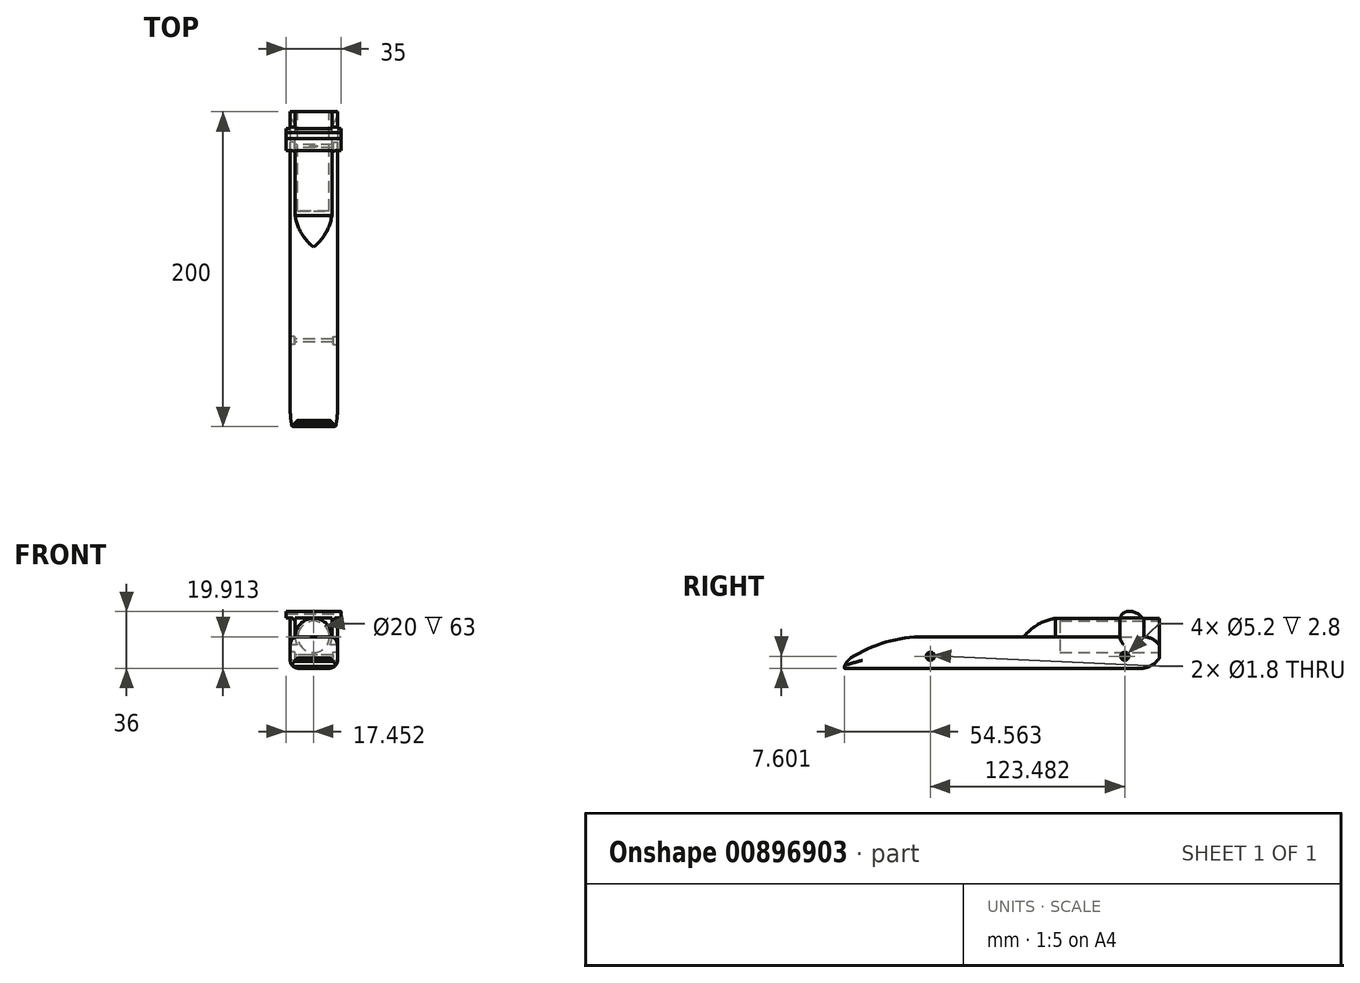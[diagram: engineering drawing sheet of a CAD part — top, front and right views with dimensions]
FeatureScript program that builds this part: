
annotation { "Feature Type Name" : "Feature", "Feature Type Description" : "" }
export const myFeature = defineFeature(function(context is Context, id is Id, definition is map)
    precondition{}
    {
        {
            var Q0;
            Q0=qCreatedBy(makeId("Right.planeOp"),FACE);
            var sketch = newSketch(context, id + "F0", { "sketchPlane" : qUnion([Q0])});
            skLineSegment(sketch, "E0.bottom", {"start": v(89.71, -10) * mm, "end": v(-37.4, -10) * mm});
            skLineSegment(sketch, "E0.top", {"start": v(90.1, 10) * mm, "end": v(-49.28, 10) * mm});
            skLineSegment(sketch, "E0.left", {"start": v(100, -3.63) * mm, "end": v(100, 4.7) * mm});
            skPoint(sketch, "E0.middle", {"position": v(0, 0) * mm});
            skArc(sketch, "E1", {"start": v(-32.94, 10) * mm, "mid": v(-41.11, 10.16) * mm, "end": v(-49.28, 10) * mm});
            skArc(sketch, "E2", {"start": v(-37.4, -10) * mm, "mid": v(-35.18, -10.01) * mm, "end": v(-32.94, -10) * mm});
            skPoint(sketch, "E3.orphan", {"position": v(-100, 10) * mm});
            skPoint(sketch, "E4.orphan", {"position": v(-100, -10) * mm});
            skCircle(sketch, "E5", {"center": v(78.04, -2.4) * mm, "radius": 0.9 * mm});
            skCircle(sketch, "E6", {"center": v(-45.44, -2.4) * mm, "radius": 0.9 * mm});
            skArc(sketch, "E7", {"start": v(100, 4.7) * mm, "mid": v(95.32, 8.7) * mm, "end": v(89.32, 10) * mm});
            skArc(sketch, "E8", {"start": v(89.71, -10) * mm, "mid": v(95.52, -7.9) * mm, "end": v(100, -3.63) * mm});
            skPoint(sketch, "E9.orphan", {"position": v(100, 10) * mm});
            skPoint(sketch, "E10.orphan", {"position": v(100, -10) * mm});
            skLineSegment(sketch, "E11", {"start": v(-37.4, -10) * mm, "end": v(-100, -10) * mm});
            skPoint(sketch, "E0.right.start.orphan", {"position": v(-100, 0) * mm});
            skArc(sketch, "E12", {"start": v(-49.28, 10) * mm, "mid": v(-75.9, 5.84) * mm, "end": v(-100, -6.23) * mm});
            skLineSegment(sketch, "E13", {"start": v(-100, -6.23) * mm, "end": v(-100, -10) * mm});
            skSolve(sketch);
        }
        {
            var Q0;
            {var subQ4=sQuery(id+"F0.wireOp",EDGE,"E0.left");Q0=makeQuery(id+"F0.imprint","IMPRINT",FACE,{"disambiguationData":[TD([[makeQuery(id+"F0.imprint","IMPRINT",EDGE,{"derivedFrom":subQ4}),1.0]])]});}
            extrude(context, id + "F1", {"entities" : qUnion([Q0]), "depth" : 30 * mm, "offsetDistance" : 25 * mm});
        }
        {
            var Q0;
            Q0=makeQuery(id+"F1.opExtrude","SWEPT_FACE",FACE,{"disambiguationData":[OSD([sQuery(id+"F0.wireOp",EDGE,"E0.left")])]});
            var sketch = newSketch(context, id + "F2", { "sketchPlane" : qUnion([Q0])});
            skCircle(sketch, "E14", {"center": v(-14.8, 9.91) * mm, "radius": 11.67 * mm});
            skSolve(sketch);
        }
        {
            var Q0;
            Q0=qSketchRegion(id+"F2",true);
            extrude(context, id + "F3", {"entities" : qUnion([Q0]), "operationType" : NewBodyOperationType.ADD, "oppositeDirection" : true, "depth" : 66 * mm, "offsetDistance" : 25 * mm});
        }
        {
            var Q0;
            Q0=makeQuery(id+"F3.opExtrude","CAP_FACE",FACE,{"disambiguationData":[OSD([sQuery(id+"F2.wireOp",EDGE,"E14")])],"isStart":true});
            var sketch = newSketch(context, id + "F4", { "sketchPlane" : qUnion([Q0])});
            skCircle(sketch, "E15", {"center": v(-14.8, 9.91) * mm, "radius": 10 * mm});
            skSolve(sketch);
        }
        {
            var Q0;
            Q0=qSketchRegion(id+"F4",true);
            extrude(context, id + "F5", {"entities" : qUnion([Q0]), "operationType" : NewBodyOperationType.REMOVE, "oppositeDirection" : true, "depth" : 63 * mm, "offsetDistance" : 25 * mm});
        }
        {
            var Q0;
            Q0=makeQuery(id+"F1.opExtrude","SWEPT_FACE",FACE,{"disambiguationData":[OSD([sQuery(id+"F0.wireOp",EDGE,"E0.top")])]});
            var sketch = newSketch(context, id + "F6", { "sketchPlane" : qUnion([Q0])});
            skLineSegment(sketch, "E16", {"start": v(14.8, 34) * mm, "end": v(14.8, 14) * mm});
            skLineSegment(sketch, "E17", {"start": v(14.8, 34) * mm, "end": v(3.15, 34) * mm});
            skArc(sketch, "E18", {"start": v(3.15, 34) * mm, "mid": v(7.06, 22.88) * mm, "end": v(14.8, 14) * mm});
            skSolve(sketch);
        }
        {
            var Q0;
            {var subQ0=sQuery(id+"F6.wireOp",EDGE,"E16");Q0=makeQuery(id+"F6.imprint","IMPRINT",FACE,{"disambiguationData":[TD([[makeQuery(id+"F6.imprint","IMPRINT",EDGE,{"derivedFrom":subQ0}),-1.0]])]});}
            var Q1;
            Q1=sQuery(id+"F6.wireOp",EDGE,"E16");
            revolve(context, id + "F7", {"operationType" : NewBodyOperationType.ADD, "surfaceOperationType" : NewSurfaceOperationType.NEW, "entities" : qUnion([Q0]), "axis" : qUnion([Q1]), "revolveType" : RevolveType.FULL});
        }
        {
            var Q0;
            Q0=makeQuery(id+"F1.opExtrude","SWEPT_EDGE",EDGE,{"disambiguationData":[OSD([sQuery(id+"F0.wireOp",EDGE,"E12"),sQuery(id+"F0.wireOp",EDGE,"E13")])]});
            chamfer(context, id + "F8", {"entities" : qUnion([Q0]), "width" : 5 * mm, "tangentPropagation" : true});
        }
        {
            var Q0;
            {var subQ0=sQuery(id+"F0.wireOp",EDGE,"E12");Q0=makeQuery(id+"F8.opChamfer","BLEND_EDGE",EDGE,{"blendedFrom":[makeQuery(id+"F1.opExtrude","SWEPT_EDGE",EDGE,{"disambiguationData":[OSD([subQ0,sQuery(id+"F0.wireOp",EDGE,"E13")])]}),makeQuery(id+"F1.opExtrude","SWEPT_FACE",FACE,{"disambiguationData":[OSD([subQ0])]})],"blendedInto":[makeQuery(id+"F1.opExtrude","SWEPT_FACE",FACE,{"disambiguationData":[OSD([subQ0])]})]});}
            chamfer(context, id + "F9", {"entities" : qUnion([Q0]), "width" : 5 * mm, "tangentPropagation" : true});
        }
        {
            var Q0;
            {var subQ0=sQuery(id+"F0.wireOp",EDGE,"E12");var subQ1=makeQuery(id+"F1.opExtrude","SWEPT_FACE",FACE,{"disambiguationData":[OSD([subQ0])]});Q0=makeQuery(id+"F9.opChamfer","BLEND_EDGE",EDGE,{"blendedFrom":[makeQuery(id+"F8.opChamfer","BLEND_EDGE",EDGE,{"blendedFrom":[makeQuery(id+"F1.opExtrude","SWEPT_EDGE",EDGE,{"disambiguationData":[OSD([subQ0,sQuery(id+"F0.wireOp",EDGE,"E13")])]}),subQ1],"blendedInto":[subQ1]}),subQ1],"blendedInto":[subQ1]});}
            chamfer(context, id + "F10", {"entities" : qUnion([Q0]), "width" : 5 * mm, "tangentPropagation" : true});
        }
        {
            var Q0;
            Q0=makeQuery(id+"F1.opExtrude","CAP_EDGE",EDGE,{"disambiguationData":[OSD([sQuery(id+"F0.wireOp",EDGE,"E0.bottom"),sQuery(id+"F0.wireOp",EDGE,"E11")])],"isStart":false});
            var Q1;
            Q1=makeQuery(id+"F1.opExtrude","CAP_EDGE",EDGE,{"disambiguationData":[OSD([sQuery(id+"F0.wireOp",EDGE,"E0.bottom"),sQuery(id+"F0.wireOp",EDGE,"E11")])],"isStart":true});
            fillet(context, id + "F11", {"entities" : qUnion([Q0, Q1]), "radius" : 5 * mm, "tangentPropagation" : true, "allowEdgeOverflow" : false});
        }
        {
            var Q0;
            Q0=makeQuery(id+"F1.opExtrude","CAP_FACE",FACE,{"disambiguationData":[OSD([sQuery(id+"F0.wireOp",EDGE,"E0.bottom"),sQuery(id+"F0.wireOp",EDGE,"E0.top"),sQuery(id+"F0.wireOp",EDGE,"E0.left"),sQuery(id+"F0.wireOp",EDGE,"E5"),sQuery(id+"F0.wireOp",EDGE,"E6"),sQuery(id+"F0.wireOp",EDGE,"E7"),sQuery(id+"F0.wireOp",EDGE,"E8"),sQuery(id+"F0.wireOp",EDGE,"E11"),sQuery(id+"F0.wireOp",EDGE,"E12"),sQuery(id+"F0.wireOp",EDGE,"E13")])],"isStart":false});
            var sketch = newSketch(context, id + "F12", { "sketchPlane" : qUnion([Q0])});
            skCircle(sketch, "E19", {"center": v(-45.44, -2.4) * mm, "radius": 2.6 * mm});
            skSolve(sketch);
        }
        {
            var Q0;
            Q0=qSketchRegion(id+"F12",true);
            extrude(context, id + "F13", {"entities" : qUnion([Q0]), "operationType" : NewBodyOperationType.REMOVE, "oppositeDirection" : true, "depth" : 2.8 * mm, "offsetDistance" : 25 * mm});
        }
        {
            var Q0;
            Q0=makeQuery(id+"F1.opExtrude","CAP_FACE",FACE,{"disambiguationData":[OSD([sQuery(id+"F0.wireOp",EDGE,"E0.bottom"),sQuery(id+"F0.wireOp",EDGE,"E0.top"),sQuery(id+"F0.wireOp",EDGE,"E0.left"),sQuery(id+"F0.wireOp",EDGE,"E5"),sQuery(id+"F0.wireOp",EDGE,"E6"),sQuery(id+"F0.wireOp",EDGE,"E7"),sQuery(id+"F0.wireOp",EDGE,"E8"),sQuery(id+"F0.wireOp",EDGE,"E11"),sQuery(id+"F0.wireOp",EDGE,"E12"),sQuery(id+"F0.wireOp",EDGE,"E13")])],"isStart":false});
            var sketch = newSketch(context, id + "F14", { "sketchPlane" : qUnion([Q0])});
            skCircle(sketch, "E20", {"center": v(78.04, -2.4) * mm, "radius": 2.6 * mm});
            skSolve(sketch);
        }
        {
            var Q0;
            Q0=qSketchRegion(id+"F14",true);
            extrude(context, id + "F15", {"entities" : qUnion([Q0]), "operationType" : NewBodyOperationType.REMOVE, "oppositeDirection" : true, "depth" : 2.8 * mm, "offsetDistance" : 25 * mm});
        }
        {
            var Q0;
            Q0=makeQuery(id+"F1.opExtrude","CAP_FACE",FACE,{"disambiguationData":[OSD([sQuery(id+"F0.wireOp",EDGE,"E0.bottom"),sQuery(id+"F0.wireOp",EDGE,"E0.top"),sQuery(id+"F0.wireOp",EDGE,"E0.left"),sQuery(id+"F0.wireOp",EDGE,"E5"),sQuery(id+"F0.wireOp",EDGE,"E6"),sQuery(id+"F0.wireOp",EDGE,"E7"),sQuery(id+"F0.wireOp",EDGE,"E8"),sQuery(id+"F0.wireOp",EDGE,"E11"),sQuery(id+"F0.wireOp",EDGE,"E12"),sQuery(id+"F0.wireOp",EDGE,"E13")])],"isStart":true});
            var sketch = newSketch(context, id + "F16", { "sketchPlane" : qUnion([Q0])});
            skCircle(sketch, "E21", {"center": v(-78.04, -2.4) * mm, "radius": 2.6 * mm});
            skSolve(sketch);
        }
        {
            var Q0;
            Q0=qSketchRegion(id+"F16",true);
            extrude(context, id + "F17", {"entities" : qUnion([Q0]), "operationType" : NewBodyOperationType.REMOVE, "oppositeDirection" : true, "depth" : 2.8 * mm, "offsetDistance" : 25 * mm});
        }
        {
            var Q0;
            Q0=makeQuery(id+"F1.opExtrude","CAP_FACE",FACE,{"disambiguationData":[OSD([sQuery(id+"F0.wireOp",EDGE,"E0.bottom"),sQuery(id+"F0.wireOp",EDGE,"E0.top"),sQuery(id+"F0.wireOp",EDGE,"E0.left"),sQuery(id+"F0.wireOp",EDGE,"E5"),sQuery(id+"F0.wireOp",EDGE,"E6"),sQuery(id+"F0.wireOp",EDGE,"E7"),sQuery(id+"F0.wireOp",EDGE,"E8"),sQuery(id+"F0.wireOp",EDGE,"E11"),sQuery(id+"F0.wireOp",EDGE,"E12"),sQuery(id+"F0.wireOp",EDGE,"E13")])],"isStart":true});
            var sketch = newSketch(context, id + "F18", { "sketchPlane" : qUnion([Q0])});
            skCircle(sketch, "E22", {"center": v(45.44, -2.4) * mm, "radius": 2.6 * mm});
            skSolve(sketch);
        }
        {
            var Q0;
            Q0=qSketchRegion(id+"F18",true);
            extrude(context, id + "F19", {"entities" : qUnion([Q0]), "operationType" : NewBodyOperationType.REMOVE, "oppositeDirection" : true, "depth" : 2.8 * mm, "offsetDistance" : 25 * mm});
        }
        {
            var Q0;
            Q0=makeQuery(id+"F1.opExtrude","SWEPT_FACE",FACE,{"disambiguationData":[OSD([sQuery(id+"F0.wireOp",EDGE,"E0.top")])]});
            var sketch = newSketch(context, id + "F20", { "sketchPlane" : qUnion([Q0])});
            skLineSegment(sketch, "E23", {"start": v(26.47, 90.1) * mm, "end": v(26.47, 75.1) * mm});
            skLineSegment(sketch, "E24", {"start": v(26.47, 75.1) * mm, "end": v(30, 75.1) * mm});
            skLineSegment(sketch, "E25", {"start": v(30, 75.1) * mm, "end": v(30, 90.1) * mm});
            skLineSegment(sketch, "E26", {"start": v(30, 90.1) * mm, "end": v(26.47, 90.1) * mm});
            skLineSegment(sketch, "E27", {"start": v(3.13, 90.1) * mm, "end": v(3.13, 75.1) * mm});
            skLineSegment(sketch, "E28", {"start": v(3.13, 75.1) * mm, "end": v(0, 75.1) * mm});
            skLineSegment(sketch, "E29", {"start": v(0, 75.1) * mm, "end": v(0, 90.1) * mm});
            skLineSegment(sketch, "E30", {"start": v(0, 90.1) * mm, "end": v(3.13, 90.1) * mm});
            skSolve(sketch);
        }
        {
            var Q0;
            Q0 = qSketchRegion(id + "F20", true);
            extrude(context, id + "F21", {"entities" : qUnion([Q0]), "operationType" : NewBodyOperationType.ADD, "depth" : 12 * mm, "offsetDistance" : 25 * mm});
        }
        {
            var Q0;
            Q0=makeQuery(id+"F21.opExtrude","SWEPT_FACE",FACE,{"disambiguationData":[OSD([sQuery(id+"F20.wireOp",EDGE,"E26")])]});
            var sketch = newSketch(context, id + "F22", { "sketchPlane" : qUnion([Q0])});
            skLineSegment(sketch, "E31", {"start": v(-32.35, 22) * mm, "end": v(2.65, 22) * mm});
            skLineSegment(sketch, "E32", {"start": v(2.65, 22) * mm, "end": v(2.65, 26) * mm});
            skLineSegment(sketch, "E33", {"start": v(2.65, 26) * mm, "end": v(-32.35, 26) * mm});
            skLineSegment(sketch, "E34", {"start": v(-32.35, 26) * mm, "end": v(-32.35, 22) * mm});
            skSolve(sketch);
        }
        {
            var Q0;
            Q0 = qSketchRegion(id + "F22", true);
            extrude(context, id + "F23", {"entities" : qUnion([Q0]), "operationType" : NewBodyOperationType.ADD, "oppositeDirection" : true, "depth" : 15 * mm, "offsetDistance" : 25 * mm});
        }
        {
            var Q0;
            Q0=makeQuery(id+"F1.opExtrude","CAP_EDGE",EDGE,{"disambiguationData":[OSD([sQuery(id+"F0.wireOp",EDGE,"E0.top")])],"isStart":false});
            var Q1;
            Q1=makeQuery(id+"F1.opExtrude","CAP_EDGE",EDGE,{"disambiguationData":[OSD([sQuery(id+"F0.wireOp",EDGE,"E0.top")])],"isStart":true});
            fillet(context, id + "F24", {"entities" : qUnion([Q0, Q1]), "radius" : 5 * mm, "tangentPropagation" : true, "allowEdgeOverflow" : false});
        }
        {
            var Q0;
            Q0=makeQuery(id+"F21.opExtrude","SWEPT_EDGE",EDGE,{"disambiguationData":[OSD([sQuery(id+"F0.wireOp",EDGE,"E0.top"),sQuery(id+"F20.wireOp",EDGE,"E24"),sQuery(id+"F20.wireOp",EDGE,"E25")])]});
            fillet(context, id + "F25", {"entities" : qUnion([Q0]), "radius" : 2 * mm, "tangentPropagation" : true, "allowEdgeOverflow" : false});
        }
        {
            var Q0;
            Q0=makeQuery(id+"F21.opExtrude","SWEPT_EDGE",EDGE,{"disambiguationData":[OSD([sQuery(id+"F0.wireOp",EDGE,"E0.top"),sQuery(id+"F20.wireOp",EDGE,"E28"),sQuery(id+"F20.wireOp",EDGE,"E29")])]});
            fillet(context, id + "F26", {"entities" : qUnion([Q0]), "radius" : 2 * mm, "tangentPropagation" : true, "allowEdgeOverflow" : false});
        }
        {
            var Q0;
            Q0=makeQuery(id+"F23.opExtrude","CAP_EDGE",EDGE,{"disambiguationData":[OSD([sQuery(id+"F22.wireOp",EDGE,"E33")])],"isStart":false});
            fillet(context, id + "F27", {"entities" : qUnion([Q0]), "radius" : 5 * mm, "tangentPropagation" : true, "allowEdgeOverflow" : false});
        }
        {
            var Q0;
            Q0=makeQuery(id+"F23.opExtrude","CAP_EDGE",EDGE,{"disambiguationData":[OSD([sQuery(id+"F22.wireOp",EDGE,"E33")])],"isStart":true});
            chamfer(context, id + "F28", {"entities" : qUnion([Q0]), "width" : 5 * mm, "tangentPropagation" : true});
        }
        {
            var Q0;
            {var subQ0=sQuery(id+"F22.wireOp",EDGE,"E33");Q0=makeQuery(id+"F28.opChamfer","BLEND_EDGE",EDGE,{"blendedFrom":[makeQuery(id+"F23.opExtrude","CAP_EDGE",EDGE,{"disambiguationData":[OSD([subQ0])],"isStart":true}),makeQuery(id+"F23.opExtrude","SWEPT_FACE",FACE,{"disambiguationData":[OSD([subQ0])]})],"blendedInto":[makeQuery(id+"F23.opExtrude","SWEPT_FACE",FACE,{"disambiguationData":[OSD([subQ0])]})]});}
            chamfer(context, id + "F29", {"entities" : qUnion([Q0]), "width" : 5 * mm, "tangentPropagation" : true});
        }
    });
